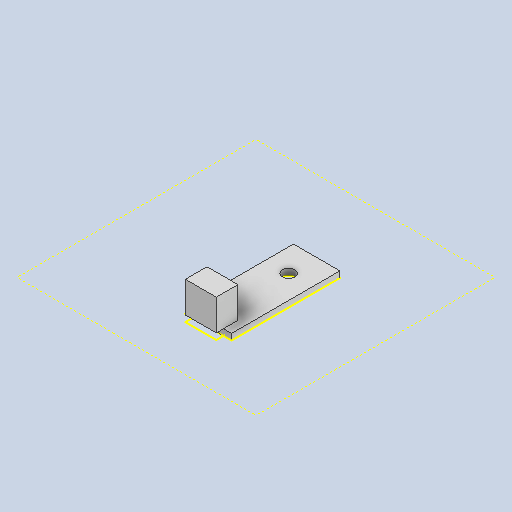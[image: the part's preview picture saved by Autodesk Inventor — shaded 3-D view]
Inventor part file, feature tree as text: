
AUTODESK INVENTOR PART (.ipt)
format: ipt  version: 2025.1 (Build 291241000, 241)  size: 93,184 bytes
history: native  units: in
note: dims shown in document units (in); Inventor stores cm internally (conversion verified against a paired STEP export)
features: other x3, sketch x1
ambient origin geometry x8: Origin, YZ Plane, XZ Plane, XY Plane, X Axis, Y Axis, Z Axis, Center Point
bodies: Solid1 (feature_tree)
feature tree (4):
  other  "Sensor ky-037.ipt"
  other  "Solid1::Sensor ky-037.ipt"
  other  "TaggingFeature1"
  sketch  "Sketch1"  dims[d0=0.3937in]
